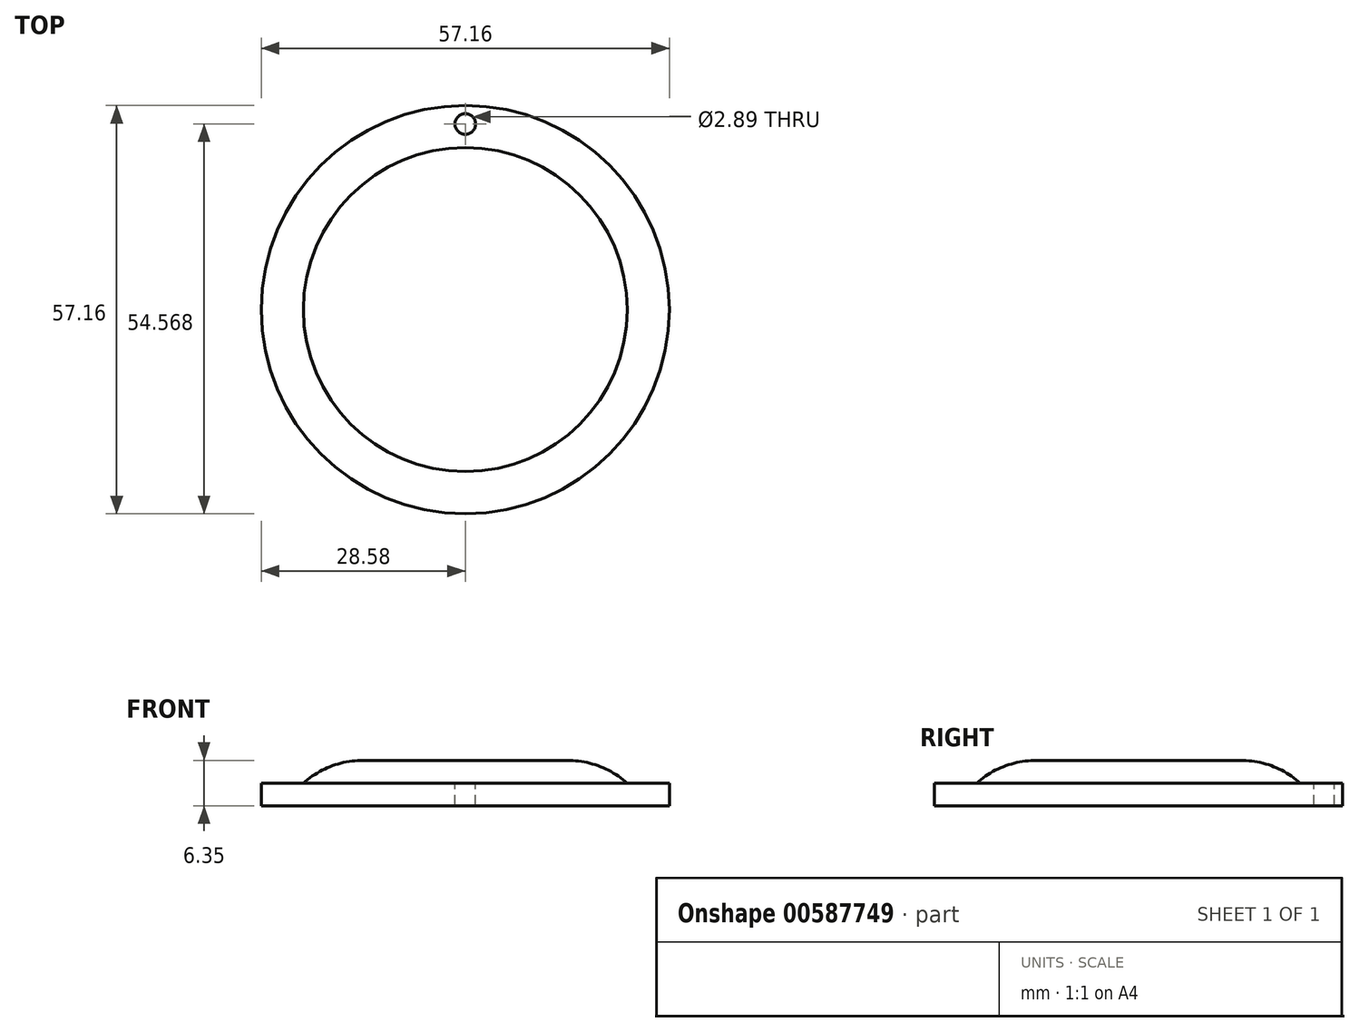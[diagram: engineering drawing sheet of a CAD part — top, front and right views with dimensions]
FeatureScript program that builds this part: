
annotation { "Feature Type Name" : "Feature", "Feature Type Description" : "" }
export const myFeature = defineFeature(function(context is Context, id is Id, definition is map)
    precondition{}
    {
        {
            var Q0;
            Q0=qCreatedBy(makeId("Top.planeOp"),FACE);
            var sketch = newSketch(context, id + "F0", { "sketchPlane" : qUnion([Q0])});
            skCircle(sketch, "E0", {"center": v(0, 0) * mm, "radius": 28.58 * mm});
            skSolve(sketch);
        }
        {
            var Q0;
            Q0=qCreatedBy(makeId("Top.planeOp"),FACE);
            var sketch = newSketch(context, id + "F1", { "sketchPlane" : qUnion([Q0])});
            skCircle(sketch, "E1", {"center": v(0, 0) * mm, "radius": 22.67 * mm});
            skSolve(sketch);
        }
        {
            var Q0;
            Q0=makeQuery(id+"F0.imprint","IMPRINT",FACE,{"disambiguationData":[TD([[makeQuery(id+"F0.imprint","IMPRINT",EDGE,{"derivedFrom":sQuery(id+"F0.wireOp",EDGE,"E0")}),1.0]])]});
            extrude(context, id + "F2", {"entities" : qUnion([Q0]), "depth" : 3.17 * mm, "offsetDistance" : 25.4 * mm});
        }
        {
            var Q0;
            Q0 = qSketchRegion(id + "F1", true);
            extrude(context, id + "F3", {"entities" : qUnion([Q0]), "operationType" : NewBodyOperationType.ADD, "depth" : 6.35 * mm, "offsetDistance" : 25.4 * mm});
        }
        {
            var Q0;
            Q0=makeQuery(id+"F3.opExtrude","CAP_FACE",FACE,{"disambiguationData":[OSD([sQuery(id+"F1.wireOp",EDGE,"E1")])],"isStart":false});
            var sketch = newSketch(context, id + "F4", { "sketchPlane" : qUnion([Q0])});
            skCircle(sketch, "E2", {"center": v(0, 25.99) * mm, "radius": 1.44 * mm});
            skSolve(sketch);
        }
        {
            var Q0;
            Q0=makeQuery(id+"F4.imprint","IMPRINT",FACE,{"disambiguationData":[TD([[makeQuery(id+"F4.imprint","IMPRINT",EDGE,{"derivedFrom":sQuery(id+"F4.wireOp",EDGE,"E2")}),1.0]])]});
            extrude(context, id + "F5", {"entities" : qUnion([Q0]), "operationType" : NewBodyOperationType.REMOVE, "endBound" : BoundingType.THROUGH_ALL, "oppositeDirection" : true, "depth" : 25.4 * mm, "offsetDistance" : 25.4 * mm});
        }
        {
            var Q0;
            Q0=makeQuery(id+"F3.opExtrude","CAP_EDGE",EDGE,{"disambiguationData":[OSD([sQuery(id+"F1.wireOp",EDGE,"E1")])],"isStart":false});
            fillet(context, id + "F6", {"entities" : qUnion([Q0]), "radius" : 12.7 * mm, "tangentPropagation" : true, "allowEdgeOverflow" : false});
        }
    });
